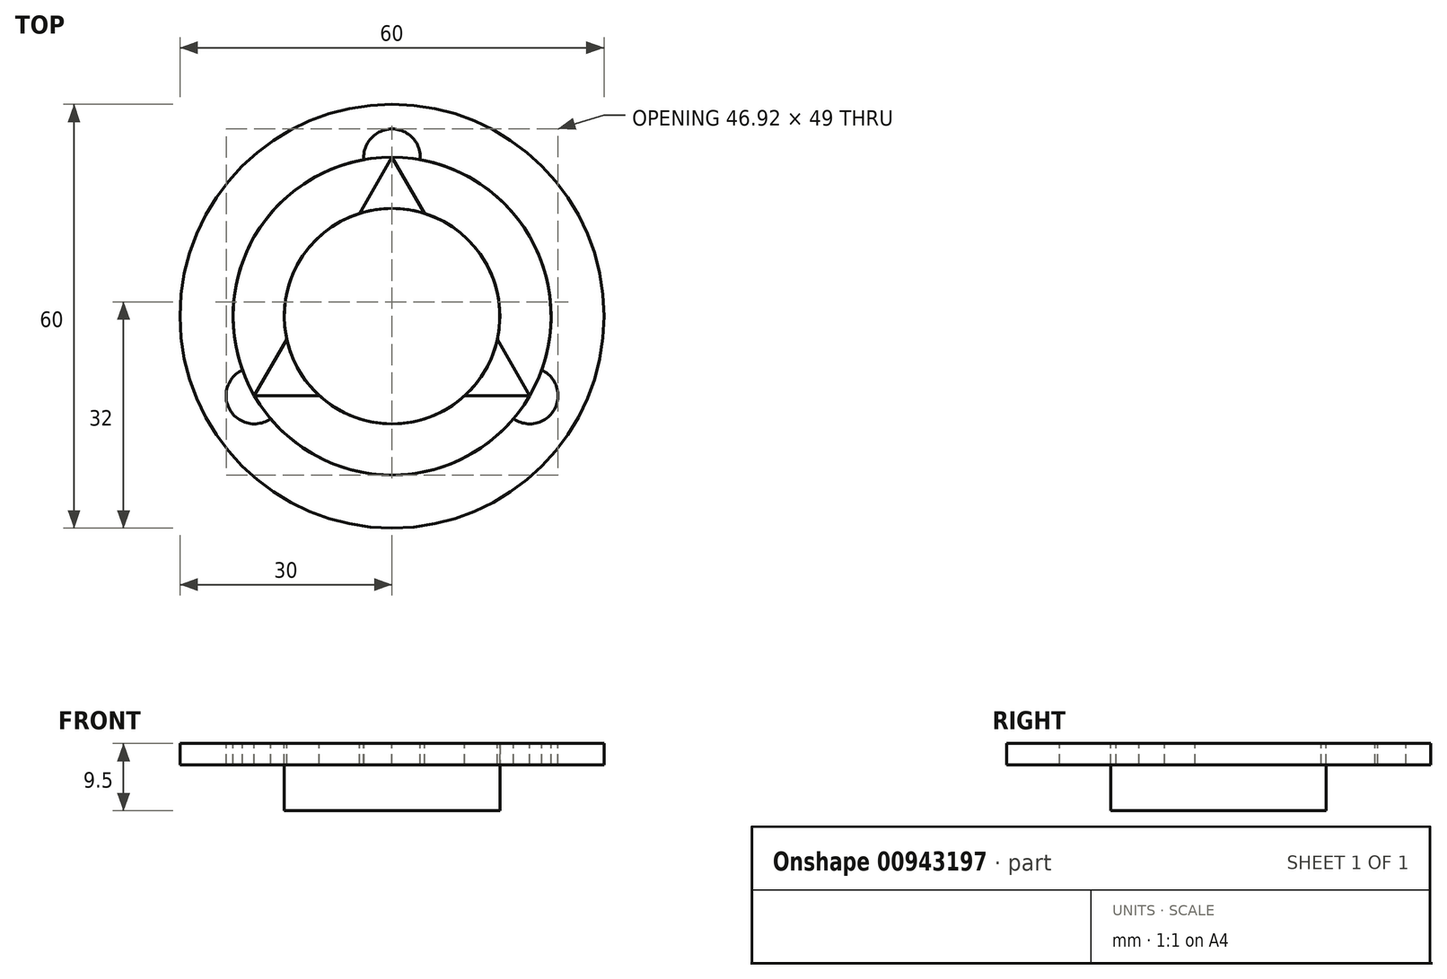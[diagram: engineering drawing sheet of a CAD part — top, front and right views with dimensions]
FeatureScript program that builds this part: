
annotation { "Feature Type Name" : "Feature", "Feature Type Description" : "" }
export const myFeature = defineFeature(function(context is Context, id is Id, definition is map)
    precondition{}
    {
        {
            var Q0;
            Q0=qCreatedBy(makeId("Top.planeOp"),FACE);
            var sketch = newSketch(context, id + "F0", { "sketchPlane" : qUnion([Q0])});
            skCircle(sketch, "E0", {"center": v(0, 0) * mm, "radius": 15.25 * mm});
            skSolve(sketch);
        }
        {
            var Q0;
            Q0=makeQuery(id+"F0.imprint","IMPRINT",FACE,{"disambiguationData":[TD([[makeQuery(id+"F0.imprint","IMPRINT",EDGE,{"derivedFrom":sQuery(id+"F0.wireOp",EDGE,"E0")}),1.0]])]});
            extrude(context, id + "F1", {"entities" : qUnion([Q0]), "depth" : 9.5 * mm, "offsetDistance" : 25 * mm});
        }
        {
            var Q0;
            Q0=makeQuery(id+"F1.opExtrude","CAP_FACE",FACE,{"disambiguationData":[OSD([sQuery(id+"F0.wireOp",EDGE,"E0")])],"isStart":false});
            var sketch = newSketch(context, id + "F2", { "sketchPlane" : qUnion([Q0])});
            skCircle(sketch, "E1", {"center": v(0, 0) * mm, "radius": 30 * mm});
            skCircle(sketch, "E2", {"center": v(0, 0) * mm, "radius": 22.5 * mm});
            skPoint(sketch, "E3", {"position": v(0, 22.5) * mm});
            skCircle(sketch, "E4.cCircle", {"center": v(0, 0) * mm, "radius": 22.5 * mm, "construction": true});
            skLineSegment(sketch, "E4.0", {"start": v(0, 22.5) * mm, "end": v(19.49, -11.25) * mm});
            skLineSegment(sketch, "E4.1", {"start": v(19.49, -11.25) * mm, "end": v(-19.49, -11.25) * mm});
            skLineSegment(sketch, "E4.2", {"start": v(-19.49, -11.25) * mm, "end": v(0, 22.5) * mm});
            skSolve(sketch);
        }
        {
            var Q0;
            Q0=makeQuery(id+"F2.imprint","IMPRINT",FACE,{"disambiguationData":[TD([[makeQuery(id+"F2.imprint","IMPRINT",EDGE,{"derivedFrom":sQuery(id+"F2.wireOp",EDGE,"E1")}),1.0]])]});
            extrude(context, id + "F3", {"entities" : qUnion([Q0]), "oppositeDirection" : true, "depth" : 3 * mm, "offsetDistance" : 25 * mm});
        }
        {
            var Q0;
            Q0=makeQuery(id+"F2.imprint","IMPRINT",FACE,{"disambiguationData":[TD([[makeQuery(id+"F2.imprint","IMPRINT",EDGE,{"derivedFrom":sQuery(id+"F2.wireOp",EDGE,"E2")}),1.0]])]});
            extrude(context, id + "F4", {"entities" : qUnion([Q0]), "oppositeDirection" : true, "depth" : 3 * mm, "offsetDistance" : 25 * mm});
        }
        {
            var Q0;
            {var subQ1=sQuery(id+"F2.wireOp",EDGE,"E4.0");var subQ3=makeQuery(id+"F1.opExtrude","CAP_EDGE",EDGE,{"disambiguationData":[OSD([sQuery(id+"F0.wireOp",EDGE,"E0")])],"isStart":false});var subQ4=makeQuery(id+"F2.imprint","INTERSECT",VERTEX,{"disambiguationData":[OD(0.0)],"derivedFrom":[subQ3,subQ1]});Q0=makeQuery(id+"F2.imprint","IMPRINT",FACE,{"disambiguationData":[TD([[makeQuery(id+"F2.imprint","IMPRINT",EDGE,{"disambiguationData":[TD([[subQ4,-1.0]])],"derivedFrom":subQ3}),-1.0]])]});}
            var Q1;
            {var subQ1=sQuery(id+"F2.wireOp",EDGE,"E4.1");var subQ3=makeQuery(id+"F1.opExtrude","CAP_EDGE",EDGE,{"disambiguationData":[OSD([sQuery(id+"F0.wireOp",EDGE,"E0")])],"isStart":false});var subQ4=makeQuery(id+"F2.imprint","INTERSECT",VERTEX,{"disambiguationData":[OD(1.0)],"derivedFrom":[subQ3,subQ1]});Q1=makeQuery(id+"F2.imprint","IMPRINT",FACE,{"disambiguationData":[TD([[makeQuery(id+"F2.imprint","IMPRINT",EDGE,{"disambiguationData":[TD([[subQ4,1.0]])],"derivedFrom":subQ3}),-1.0]])]});}
            var Q2;
            {var subQ1=sQuery(id+"F2.wireOp",EDGE,"E4.0");var subQ3=makeQuery(id+"F1.opExtrude","CAP_EDGE",EDGE,{"disambiguationData":[OSD([sQuery(id+"F0.wireOp",EDGE,"E0")])],"isStart":false});var subQ4=makeQuery(id+"F2.imprint","INTERSECT",VERTEX,{"disambiguationData":[OD(1.0)],"derivedFrom":[subQ3,subQ1]});Q2=makeQuery(id+"F2.imprint","IMPRINT",FACE,{"disambiguationData":[TD([[makeQuery(id+"F2.imprint","IMPRINT",EDGE,{"disambiguationData":[TD([[subQ4,1.0]])],"derivedFrom":subQ3}),-1.0]])]});}
            extrude(context, id + "F5", {"entities" : qUnion([Q0, Q1, Q2]), "oppositeDirection" : true, "depth" : 3 * mm, "offsetDistance" : 25 * mm});
        }
        {
            var Q0;
            Q0=sQuery(id+"F2.wireOp",VERTEX,"E4.1.end");
            var Q1;
            Q1=makeQuery(id+"F3.opExtrude","SWEPT_BODY",BODY,{"disambiguationData":[OSD([sQuery(id+"F2.wireOp",EDGE,"E1"),sQuery(id+"F2.wireOp",EDGE,"E2")])]});
            hole(context, id + "F6", {"style" : HoleStyle.SIMPLE, "endStyle" : HoleEndStyle.BLIND, "holeDiameter" : 8 * mm, "majorDiameter" : 5 * mm, "holeDepth" : 5 * mm, "isTappedThrough" : true, "tappedDepth" : 12 * mm, "tapClearance" : 3, "locations" : qUnion([Q0]), "scope" : qUnion([Q1])});
        }
        {
            var Q0;
            Q0=sQuery(id+"F2.wireOp",VERTEX,"E4.0.start");
            var Q1;
            Q1=makeQuery(id+"F3.opExtrude","SWEPT_BODY",BODY,{"disambiguationData":[OSD([sQuery(id+"F2.wireOp",EDGE,"E1"),sQuery(id+"F2.wireOp",EDGE,"E2")])]});
            hole(context, id + "F7", {"style" : HoleStyle.SIMPLE, "endStyle" : HoleEndStyle.BLIND, "holeDiameter" : 8 * mm, "majorDiameter" : 5 * mm, "holeDepth" : 5 * mm, "isTappedThrough" : true, "tappedDepth" : 12 * mm, "tapClearance" : 3, "locations" : qUnion([Q0]), "scope" : qUnion([Q1])});
        }
        {
            var Q0;
            Q0=sQuery(id+"F2.wireOp",VERTEX,"E4.0.end");
            var Q1;
            Q1=makeQuery(id+"F3.opExtrude","SWEPT_BODY",BODY,{"disambiguationData":[OSD([sQuery(id+"F2.wireOp",EDGE,"E1"),sQuery(id+"F2.wireOp",EDGE,"E2")])]});
            hole(context, id + "F8", {"style" : HoleStyle.SIMPLE, "endStyle" : HoleEndStyle.BLIND, "holeDiameter" : 8 * mm, "majorDiameter" : 5 * mm, "holeDepth" : 5 * mm, "isTappedThrough" : true, "tappedDepth" : 12 * mm, "tapClearance" : 3, "locations" : qUnion([Q0]), "scope" : qUnion([Q1])});
        }
        {
            var Q0;
            Q0=sQuery(id+"F2.wireOp",VERTEX,"E1.center");
            var Q1;
            Q1=makeQuery(id+"F3.opExtrude","SWEPT_BODY",BODY,{"disambiguationData":[OSD([sQuery(id+"F2.wireOp",EDGE,"E1"),sQuery(id+"F2.wireOp",EDGE,"E2")])]});
            hole(context, id + "F9", {"style" : HoleStyle.C_BORE, "endStyle" : HoleEndStyle.BLIND, "holeDiameter" : 20 * mm, "cBoreDiameter" : 27.5 * mm, "cBoreDepth" : 6.5 * mm, "majorDiameter" : 5 * mm, "holeDepth" : 50 * mm, "isTappedThrough" : true, "tappedDepth" : 12 * mm, "tapClearance" : 3, "locations" : qUnion([Q0]), "scope" : qUnion([Q1])});
        }
    });
